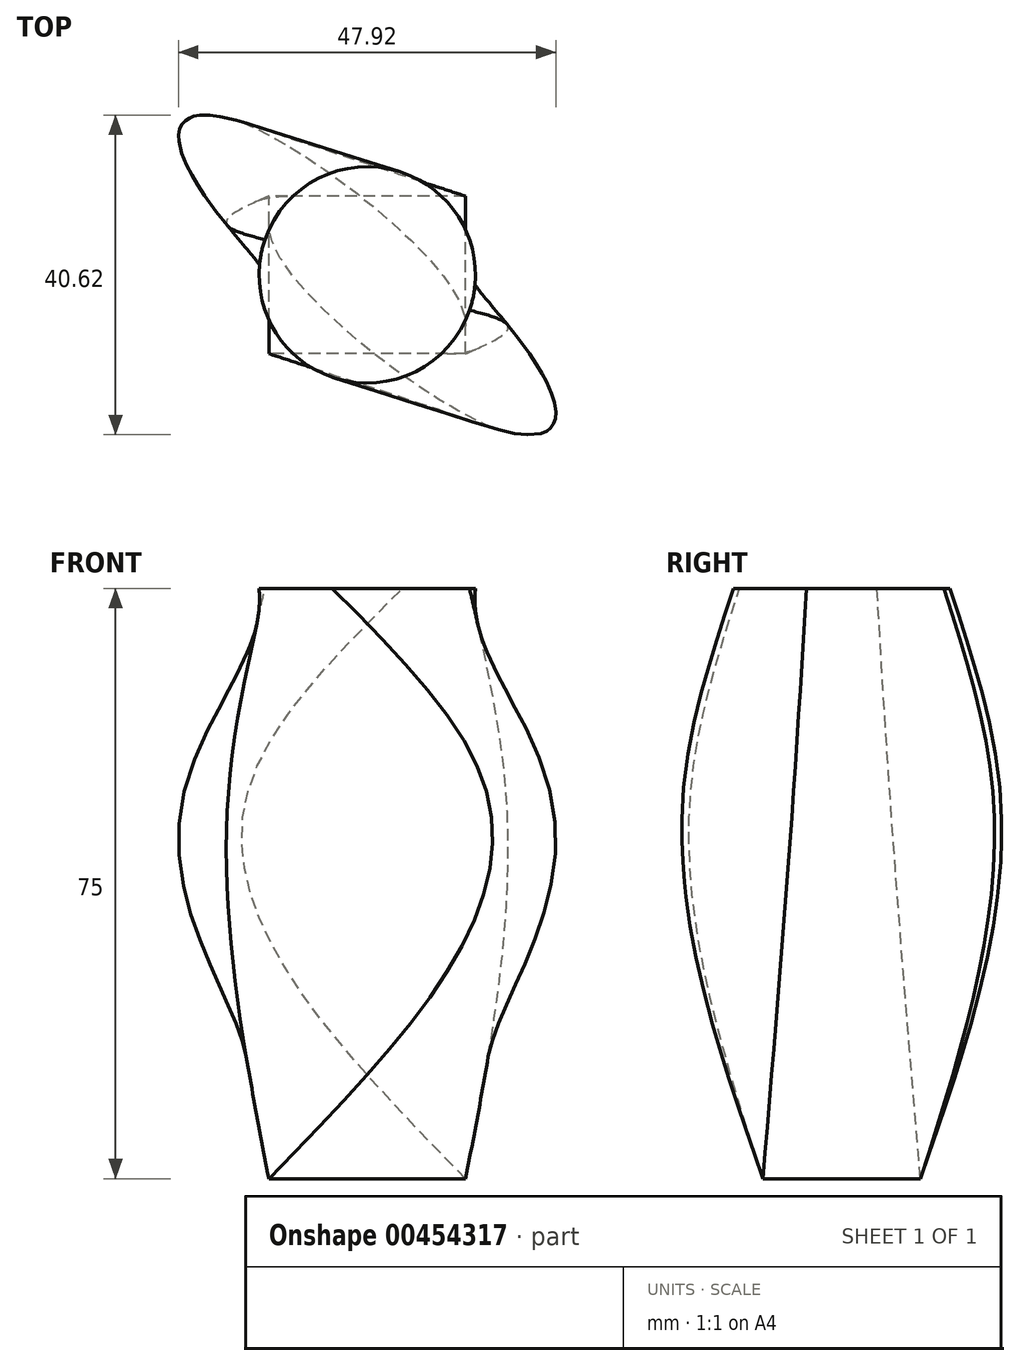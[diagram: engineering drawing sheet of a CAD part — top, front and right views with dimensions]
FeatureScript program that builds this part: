
annotation { "Feature Type Name" : "Feature", "Feature Type Description" : "" }
export const myFeature = defineFeature(function(context is Context, id is Id, definition is map)
    precondition{}
    {
        {
            var Q0;
            Q0=qCreatedBy(makeId("Top.planeOp"),FACE);
            var sketch = newSketch(context, id + "F0", { "sketchPlane" : qUnion([Q0])});
            skLineSegment(sketch, "E0.bottom", {"start": v(12.5, -10) * mm, "end": v(-12.5, -10) * mm});
            skLineSegment(sketch, "E0.top", {"start": v(12.5, 10) * mm, "end": v(-12.5, 10) * mm});
            skLineSegment(sketch, "E0.left", {"start": v(12.5, -10) * mm, "end": v(12.5, 10) * mm});
            skLineSegment(sketch, "E0.right", {"start": v(-12.5, -10) * mm, "end": v(-12.5, 10) * mm});
            skPoint(sketch, "E0.middle", {"position": v(0, 0) * mm});
            skSolve(sketch);
        }
        {
            var Q0;
            Q0=qCreatedBy(makeId("Top.planeOp"),FACE);
            cPlane(context, id + "F1", {"entities" : qUnion([Q0]), "cplaneType" : CPlaneType.OFFSET, "offset" : 50 * mm, "width" : 150 * mm, "height" : 150 * mm});
        }
        {
            var Q0;
            Q0=qCreatedBy(id+"F1.planeOp",FACE);
            var sketch = newSketch(context, id + "F2", { "sketchPlane" : qUnion([Q0])});
            skEllipse(sketch, "E1", {"center": v(0, 0) * mm, "majorRadius": 29.37 * mm, "minorRadius": 8.35 * mm, "majorAxis": v(0.76, -0.65)});
            skSolve(sketch);
        }
        {
            var Q0;
            Q0=qCreatedBy(id+"F1.planeOp",FACE);
            cPlane(context, id + "F3", {"entities" : qUnion([Q0]), "cplaneType" : CPlaneType.OFFSET, "offset" : 25 * mm, "width" : 150 * mm, "height" : 150 * mm});
        }
        {
            var Q0;
            Q0=qCreatedBy(id+"F3.planeOp",FACE);
            var sketch = newSketch(context, id + "F4", { "sketchPlane" : qUnion([Q0])});
            skCircle(sketch, "E2", {"center": v(0, 0) * mm, "radius": 13.74 * mm});
            skSolve(sketch);
        }
        {
            var Q0;
            Q0=makeQuery(id+"F0.imprint","IMPRINT",FACE,{"disambiguationData":[TD([[makeQuery(id+"F0.imprint","IMPRINT",EDGE,{"derivedFrom":sQuery(id+"F0.wireOp",EDGE,"E0.bottom")}),-1.0]])]});
            var Q1;
            Q1=makeQuery(id+"F2.imprint","IMPRINT",FACE,{"disambiguationData":[TD([[makeQuery(id+"F2.imprint","IMPRINT",EDGE,{"derivedFrom":sQuery(id+"F2.wireOp",EDGE,"E1")}),1.0]])]});
            var Q2;
            Q2=makeQuery(id+"F4.imprint","IMPRINT",FACE,{"disambiguationData":[TD([[makeQuery(id+"F4.imprint","IMPRINT",EDGE,{"derivedFrom":sQuery(id+"F4.wireOp",EDGE,"E2")}),1.0]])]});
            loft(context, id + "F5", {"sheetProfilesArray" : [{ "sheetProfileEntities" : qUnion([Q0]) }, { "sheetProfileEntities" : qUnion([Q1]) }, { "sheetProfileEntities" : qUnion([Q2]) }]});
        }
    });
